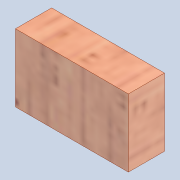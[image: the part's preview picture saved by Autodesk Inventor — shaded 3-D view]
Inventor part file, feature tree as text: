
AUTODESK INVENTOR PART (.ipt)
format: ipt  version: 2020 (Build 240168000, 168)  size: 99,328 bytes
history: native  units: mm
features: extrude x1, sketch x1
ambient origin geometry x8: Origin, YZ Plane, XZ Plane, XY Plane, X Axis, Y Axis, Z Axis, Center Point
bodies: Solid1 (feature_tree)
feature tree (2):
  extrude  "Extrusion1"  Depth=25.0mm
  sketch  "Sketch1"  dims[d0=15.0mm d1=25.0mm d2=8.0mm d3=0.0mm]
